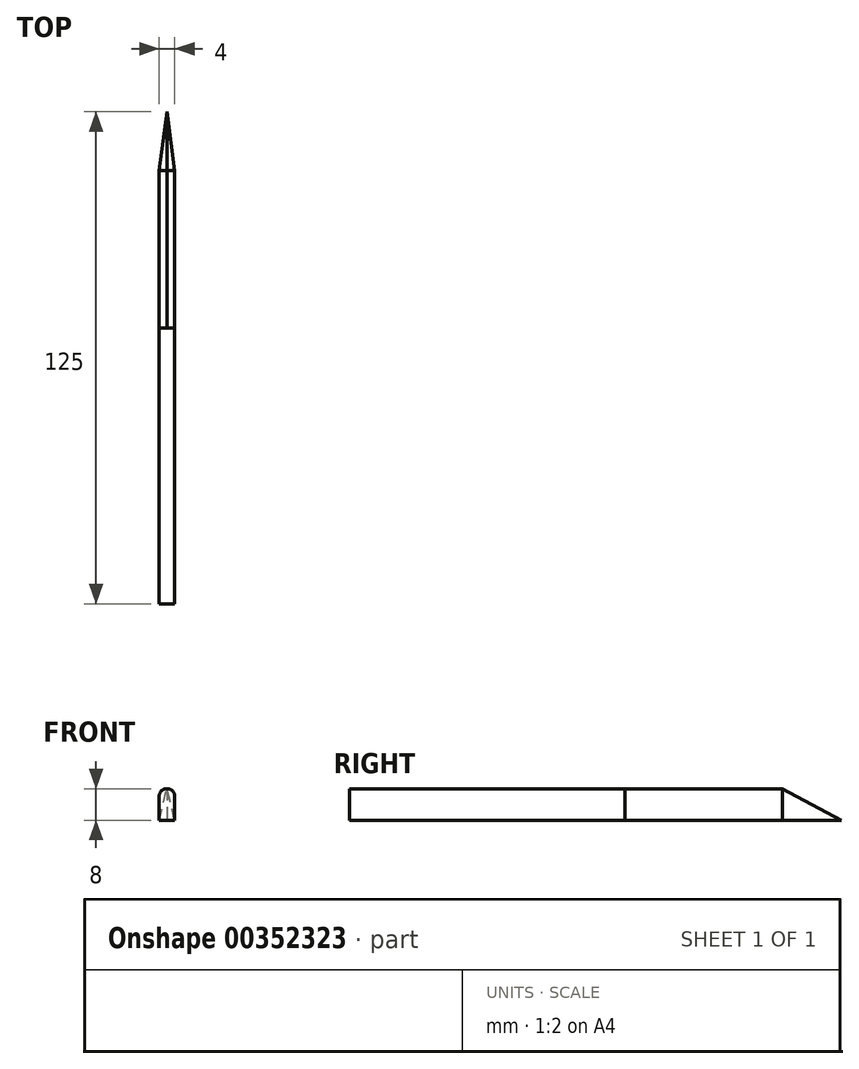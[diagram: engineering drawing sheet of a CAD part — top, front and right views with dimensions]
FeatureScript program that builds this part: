
annotation { "Feature Type Name" : "Feature", "Feature Type Description" : "" }
export const myFeature = defineFeature(function(context is Context, id is Id, definition is map)
    precondition{}
    {
        {
            var Q0;
            Q0=qCreatedBy(makeId("Front.planeOp"),FACE);
            var sketch = newSketch(context, id + "F0", { "sketchPlane" : qUnion([Q0])});
            skLineSegment(sketch, "E0", {"start": v(-2, 0) * mm, "end": v(2, 0) * mm});
            skLineSegment(sketch, "E1", {"start": v(0, 0) * mm, "end": v(0, 8) * mm, "construction": true});
            skLineSegment(sketch, "E2", {"start": v(-2, 0) * mm, "end": v(0, 8) * mm});
            skLineSegment(sketch, "E3", {"start": v(2, 0) * mm, "end": v(0, 8) * mm});
            skSolve(sketch);
        }
        {
            var Q0;
            Q0=makeQuery(id+"F0.imprint","IMPRINT",FACE,{"disambiguationData":[TD([[makeQuery(id+"F0.imprint","IMPRINT",EDGE,{"derivedFrom":sQuery(id+"F0.wireOp",EDGE,"E0")}),1.0]])]});
            extrude(context, id + "F1", {"entities" : qUnion([Q0]), "oppositeDirection" : true, "depth" : 40 * mm});
        }
        {
            var Q0;
            Q0=qCreatedBy(makeId("Top.planeOp"),FACE);
            var sketch = newSketch(context, id + "F2", { "sketchPlane" : qUnion([Q0])});
            skPoint(sketch, "E4.0", {"position": v(0, 40) * mm});
            skLineSegment(sketch, "E5.0", {"start": v(-2, 40) * mm, "end": v(2, 40) * mm});
            skLineSegment(sketch, "E6", {"start": v(0, 40) * mm, "end": v(0, 55) * mm, "construction": true});
            skLineSegment(sketch, "E7", {"start": v(0, 55) * mm, "end": v(-2, 40) * mm});
            skLineSegment(sketch, "E8", {"start": v(2, 40) * mm, "end": v(0, 55) * mm});
            skSolve(sketch);
        }
        {
            var Q0;
            Q0=makeQuery(id+"F1.opExtrude","CAP_FACE",FACE,{"disambiguationData":[OSD([sQuery(id+"F0.wireOp",EDGE,"E0"),sQuery(id+"F0.wireOp",EDGE,"E2"),sQuery(id+"F0.wireOp",EDGE,"E3")])],"isStart":false});
            var Q1;
            Q1=makeQuery(id+"F2.imprint","IMPRINT",FACE,{"disambiguationData":[TD([[makeQuery(id+"F2.imprint","IMPRINT",EDGE,{"derivedFrom":sQuery(id+"F2.wireOp",EDGE,"E5.0")}),1.0]])]});
            var Q2;
            Q2=sQuery(id+"F2.wireOp",VERTEX,"E8.end");
            var Q3;
            Q3=makeQuery(id+"F1.opExtrude","CAP_VERTEX",VERTEX,{"disambiguationData":[OSD([sQuery(id+"F0.wireOp",EDGE,"E2"),sQuery(id+"F0.wireOp",EDGE,"E3")])],"isStart":false});
            loft(context, id + "F3", {"sheetProfilesArray" : [{ "sheetProfileEntities" : qUnion([Q0]) }, { "sheetProfileEntities" : qUnion([Q1]) }], "matchConnections" : true, "connections" : [{ "connectionEntities" : qUnion([Q2, Q3]), "connectionEdgeQueries" : qUnion([]), "connectionEdgeParameters" : [] }]});
        }
        {
            var Q0;
            Q0=makeQuery(id+"F1.opExtrude","CAP_FACE",FACE,{"disambiguationData":[OSD([sQuery(id+"F0.wireOp",EDGE,"E0"),sQuery(id+"F0.wireOp",EDGE,"E2"),sQuery(id+"F0.wireOp",EDGE,"E3")])],"isStart":true});
            var sketch = newSketch(context, id + "F4", { "sketchPlane" : qUnion([Q0])});
            skLineSegment(sketch, "E9.bottom", {"start": v(-2, 0) * mm, "end": v(2, 0) * mm});
            skLineSegment(sketch, "E9.top", {"start": v(-2, 0) * mm, "end": v(2, 0) * mm});
            skLineSegment(sketch, "E9.left", {"start": v(-2, 0) * mm, "end": v(-2, 0) * mm});
            skLineSegment(sketch, "E9.right", {"start": v(2, 0) * mm, "end": v(2, 0) * mm});
            skLineSegment(sketch, "E10.bottom", {"start": v(2, 0) * mm, "end": v(-2, 0) * mm});
            skLineSegment(sketch, "E10.top", {"start": v(0, 8) * mm, "end": v(0, 8) * mm});
            skLineSegment(sketch, "E10.left", {"start": v(2, 0) * mm, "end": v(2, 6) * mm});
            skLineSegment(sketch, "E10.right", {"start": v(-2, 0) * mm, "end": v(-2, 6) * mm});
            skPoint(sketch, "E11.visualSharp", {"position": v(-2, 8) * mm});
            skArc(sketch, "E11.filletArc", {"start": v(0, 8) * mm, "mid": v(-1.41, 7.41) * mm, "end": v(-2, 6) * mm});
            skPoint(sketch, "E12.visualSharp", {"position": v(2, 8) * mm});
            skArc(sketch, "E12.filletArc", {"start": v(2, 6) * mm, "mid": v(1.41, 7.41) * mm, "end": v(0, 8) * mm});
            skSolve(sketch);
        }
        {
            var Q0;
            Q0=makeQuery(id+"F4.imprint","IMPRINT",FACE,{"disambiguationData":[TD([[makeQuery(id+"F4.imprint","IMPRINT",EDGE,{"derivedFrom":sQuery(id+"F4.wireOp",EDGE,"E10.right")}),-1.0]])]});
            var Q1;
            Q1=makeQuery(id+"F4.imprint","IMPRINT",FACE,{"disambiguationData":[TD([[makeQuery(id+"F4.imprint","IMPRINT",EDGE,{"derivedFrom":sQuery(id+"F4.wireOp",EDGE,"E10.bottom")}),1.0]])]});
            var Q2;
            Q2=makeQuery(id+"F4.imprint","IMPRINT",FACE,{"disambiguationData":[TD([[makeQuery(id+"F4.imprint","IMPRINT",EDGE,{"derivedFrom":sQuery(id+"F4.wireOp",EDGE,"E10.left")}),1.0]])]});
            var Q3;
            Q3=makeQuery(id+"F1.opExtrude","CAP_FACE",FACE,{"disambiguationData":[OSD([sQuery(id+"F0.wireOp",EDGE,"E0"),sQuery(id+"F0.wireOp",EDGE,"E2"),sQuery(id+"F0.wireOp",EDGE,"E3")])],"isStart":true});
            extrude(context, id + "F5", {"entities" : qUnion([Q0, Q1, Q2, Q3]), "operationType" : NewBodyOperationType.ADD, "depth" : 70 * mm});
        }
    });
